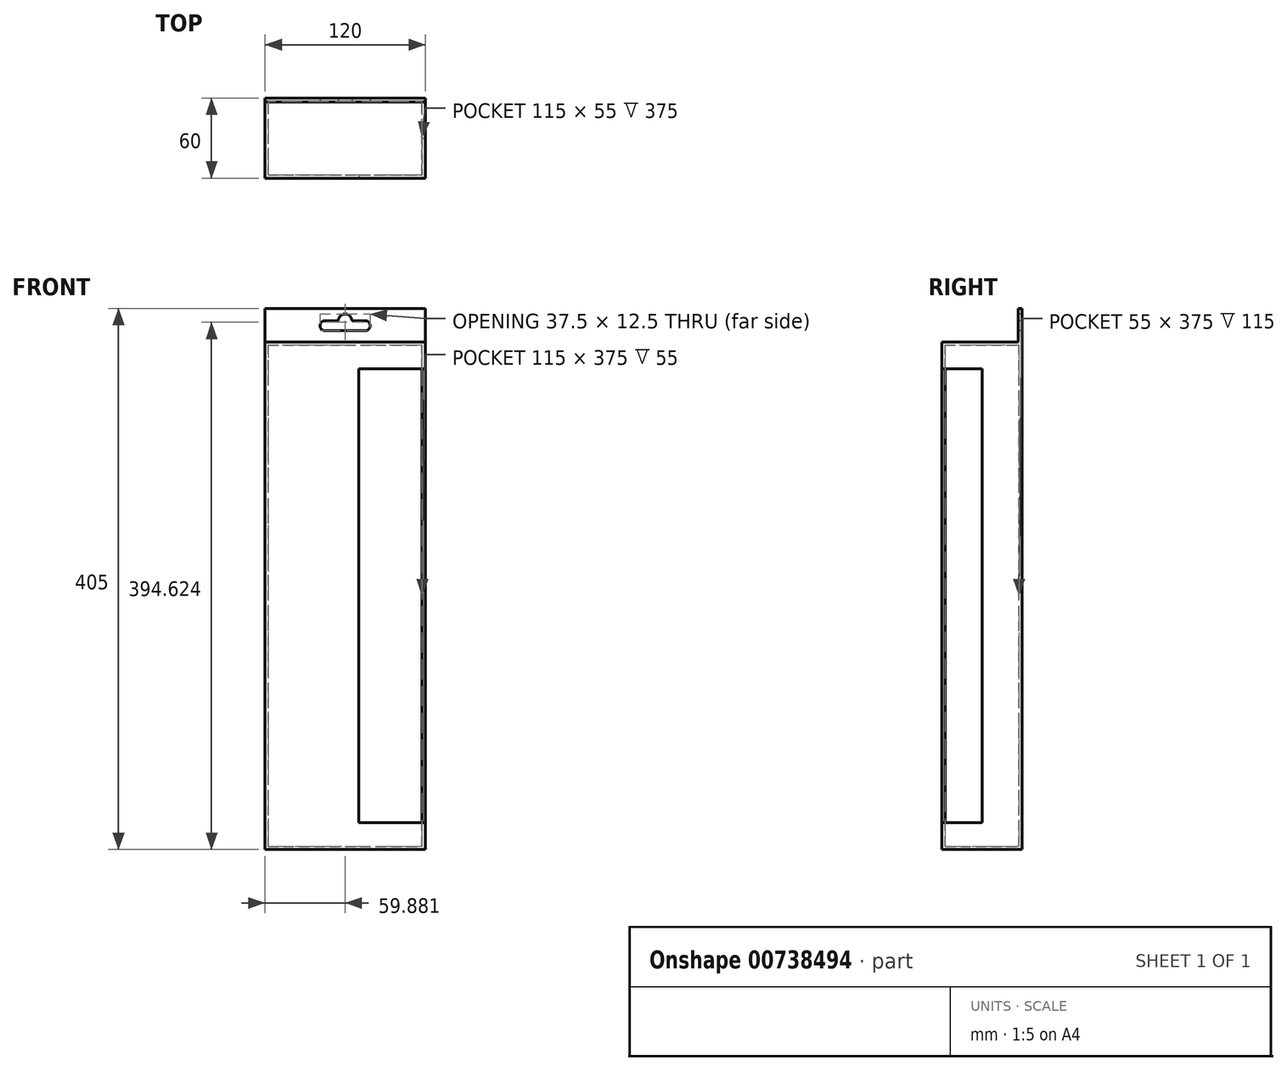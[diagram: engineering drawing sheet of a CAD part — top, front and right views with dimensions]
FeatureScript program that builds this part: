
annotation { "Feature Type Name" : "Feature", "Feature Type Description" : "" }
export const myFeature = defineFeature(function(context is Context, id is Id, definition is map)
    precondition{}
    {
        {
            var Q0;
            Q0=qCreatedBy(makeId("Front.planeOp"),FACE);
            var sketch = newSketch(context, id + "F0", { "sketchPlane" : qUnion([Q0])});
            skLineSegment(sketch, "E0.bottom", {"start": v(0, 0) * mm, "end": v(120, 0) * mm});
            skLineSegment(sketch, "E0.top", {"start": v(0, 380) * mm, "end": v(120, 380) * mm});
            skLineSegment(sketch, "E0.left", {"start": v(0, 0) * mm, "end": v(0, 380) * mm});
            skLineSegment(sketch, "E0.right", {"start": v(120, 0) * mm, "end": v(120, 380) * mm});
            skSolve(sketch);
        }
        {
            var Q0;
            Q0 = qSketchRegion(id + "F0", true);
            extrude(context, id + "F1", {"entities" : qUnion([Q0]), "depth" : 60 * mm, "offsetDistance" : 25 * mm});
        }
        {
            var Q0;
            Q0=makeQuery(id+"F1.opExtrude","CAP_FACE",FACE,{"disambiguationData":[OSD([sQuery(id+"F0.wireOp",EDGE,"E0.bottom"),sQuery(id+"F0.wireOp",EDGE,"E0.top"),sQuery(id+"F0.wireOp",EDGE,"E0.left"),sQuery(id+"F0.wireOp",EDGE,"E0.right")])],"isStart":false});
            var sketch = newSketch(context, id + "F2", { "sketchPlane" : qUnion([Q0])});
            skPoint(sketch, "E1.middle.positionSnap0", {"position": v(120, 190) * mm});
            skPoint(sketch, "E1.centerSnap0", {"position": v(120, 190) * mm});
            skLineSegment(sketch, "E2.bottom", {"start": v(70, 360) * mm, "end": v(170, 360) * mm});
            skLineSegment(sketch, "E2.top", {"start": v(70, 20) * mm, "end": v(170, 20) * mm});
            skLineSegment(sketch, "E2.left", {"start": v(70, 360) * mm, "end": v(70, 20) * mm});
            skLineSegment(sketch, "E2.right", {"start": v(170, 360) * mm, "end": v(170, 20) * mm});
            skSolve(sketch);
        }
        {
            var Q0;
            {var subQ0=sQuery(id+"F2.wireOp",EDGE,"E2.right");Q0=makeQuery(id+"F2.imprint","IMPRINT",FACE,{"disambiguationData":[TD([[makeQuery(id+"F2.imprint","IMPRINT",EDGE,{"derivedFrom":subQ0}),-1.0]])]});}
            var Q1;
            {var subQ0=sQuery(id+"F2.wireOp",EDGE,"E2.left");Q1=makeQuery(id+"F2.imprint","IMPRINT",FACE,{"disambiguationData":[TD([[makeQuery(id+"F2.imprint","IMPRINT",EDGE,{"derivedFrom":subQ0}),1.0]])]});}
            extrude(context, id + "F3", {"entities" : qUnion([Q0, Q1]), "operationType" : NewBodyOperationType.REMOVE, "oppositeDirection" : true, "depth" : 30 * mm, "offsetDistance" : 25 * mm});
        }
        {
            var Q0;
            Q0=makeQuery(id+"F3.boolean.opBoolean","COPY",FACE,{"derivedFrom":makeQuery(id+"F3.opExtrude","SWEPT_FACE",FACE,{"disambiguationData":[OSD([sQuery(id+"F2.wireOp",EDGE,"E2.top")])]})});
            var Q1;
            Q1=makeQuery(id+"F3.boolean.opBoolean","COPY",FACE,{"derivedFrom":makeQuery(id+"F3.opExtrude","CAP_FACE",FACE,{"disambiguationData":[OSD([sQuery(id+"F2.wireOp",EDGE,"E2.bottom"),sQuery(id+"F2.wireOp",EDGE,"E2.top"),sQuery(id+"F2.wireOp",EDGE,"E2.left"),sQuery(id+"F2.wireOp",EDGE,"E2.right")])],"isStart":false})});
            var Q2;
            Q2=makeQuery(id+"F3.boolean.opBoolean","COPY",FACE,{"derivedFrom":makeQuery(id+"F3.opExtrude","SWEPT_FACE",FACE,{"disambiguationData":[OSD([sQuery(id+"F2.wireOp",EDGE,"E2.left")])]})});
            var Q3;
            Q3=makeQuery(id+"F3.boolean.opBoolean","COPY",FACE,{"derivedFrom":makeQuery(id+"F3.opExtrude","SWEPT_FACE",FACE,{"disambiguationData":[OSD([sQuery(id+"F2.wireOp",EDGE,"E2.bottom")])]})});
            shell(context, id + "F4", {"entities" : qUnion([Q0, Q1, Q2, Q3]), "thickness" : 2.5 * mm});
        }
        {
            var Q0;
            Q0=makeQuery(id+"F1.opExtrude","SWEPT_FACE",FACE,{"disambiguationData":[OSD([sQuery(id+"F0.wireOp",EDGE,"E0.top")])]});
            var sketch = newSketch(context, id + "F5", { "sketchPlane" : qUnion([Q0])});
            skLineSegment(sketch, "E3.bottom", {"start": v(120, 0) * mm, "end": v(0, 0) * mm});
            skLineSegment(sketch, "E3.top", {"start": v(120, -3) * mm, "end": v(0, -3) * mm});
            skLineSegment(sketch, "E3.left", {"start": v(120, 0) * mm, "end": v(120, -3) * mm});
            skLineSegment(sketch, "E3.right", {"start": v(0, 0) * mm, "end": v(0, -3) * mm});
            skSolve(sketch);
        }
        {
            var Q0;
            Q0 = qSketchRegion(id + "F5", true);
            extrude(context, id + "F6", {"entities" : qUnion([Q0]), "operationType" : NewBodyOperationType.ADD, "depth" : 25 * mm, "offsetDistance" : 25 * mm});
        }
        {
            var Q0;
            Q0=makeQuery(id+"F6.opExtrude","SWEPT_FACE",FACE,{"disambiguationData":[OSD([sQuery(id+"F5.wireOp",EDGE,"E3.top")])]});
            var sketch = newSketch(context, id + "F7", { "sketchPlane" : qUnion([Q0])});
            skLineSegment(sketch, "E4", {"start": v(60, 405) * mm, "end": v(60.18, 391.17) * mm});
            skLineSegment(sketch, "E5.bottom", {"start": v(74.88, 395.87) * mm, "end": v(64.88, 395.87) * mm});
            skLineSegment(sketch, "E5.top", {"start": v(74.88, 388.37) * mm, "end": v(44.88, 388.37) * mm});
            skArc(sketch, "E6", {"start": v(44.88, 395.87) * mm, "mid": v(41.13, 392.12) * mm, "end": v(44.88, 388.37) * mm});
            skArc(sketch, "E7", {"start": v(74.88, 388.37) * mm, "mid": v(78.63, 392.12) * mm, "end": v(74.88, 395.87) * mm});
            skLineSegment(sketch, "E8.trimOffspring", {"start": v(54.88, 395.87) * mm, "end": v(44.88, 395.87) * mm});
            skArc(sketch, "E9", {"start": v(64.88, 395.87) * mm, "mid": v(59.88, 400.87) * mm, "end": v(54.88, 395.87) * mm});
            skSolve(sketch);
        }
        {
            var Q0;
            {var subQ0=sQuery(id+"F7.wireOp",EDGE,"E5.bottom");Q0=makeQuery(id+"F7.imprint","IMPRINT",FACE,{"disambiguationData":[TD([[makeQuery(id+"F7.imprint","IMPRINT",EDGE,{"derivedFrom":subQ0}),1.0]])]});}
            extrude(context, id + "F8", {"entities" : qUnion([Q0]), "operationType" : NewBodyOperationType.REMOVE, "oppositeDirection" : true, "depth" : 25 * mm, "offsetDistance" : 25 * mm});
        }
    });
